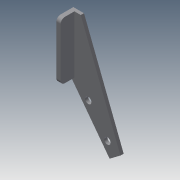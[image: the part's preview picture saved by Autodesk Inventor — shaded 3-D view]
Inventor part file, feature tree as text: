
AUTODESK INVENTOR PART (.ipt)
format: ipt  version: 2013 (Build 170138000, 138)  size: 157,184 bytes
history: native  units: mm
features: sketch x13, extrude x8, fillet x2
ambient origin geometry x8: Origin, YZ Plane, XZ Plane, XY Plane, X Axis, Y Axis, Z Axis, Center Point
bodies: Solid1 (feature_tree)
feature tree (23):
  sketch  "Sketch1"  dims[d4=3.0mm d5=3.0mm d6=2.0mm d7=0.0mm]
  extrude  "Extrusion1"  Depth=2.0mm TaperAngle=0.0deg
  extrude  "Extrusion2"  Depth=2.0mm TaperAngle=0.0deg
  extrude  "Extrusion3"  Depth=2.0mm TaperAngle=0.0deg
  sketch  "Sketch5"  dims[d19=0.5mm d20=0.0mm d21=10.0mm]
  extrude  "Extrusion4"  Depth=6.0mm TaperAngle=0.0deg
  sketch  "Sketch7"  dims[d25=1.5mm d26=0.0mm d27=10.0mm d28=0.0mm]
  sketch  "Sketch8"  dims[d29=2.0mm d30=2.0mm]
  extrude  "Extrusion5"  Depth=10.0mm
  sketch  "Sketch10"
  extrude  "Extrusion6"  Depth=1.5mm TaperAngle=0.0deg
  extrude  "Extrusion7"  Depth=10.0mm TaperAngle=0.0deg
  extrude  "Extrusion8"  Depth=2.0mm
  fillet  "Fillet1"  [1 undecoded]
  fillet  "Fillet2"  [1 undecoded]
  sketch  "Sketch2"  dims[d8=10.0mm d11=2.0mm d12=0.0mm]
  sketch  "Sketch3"  dims[d13=5.0mm d14=2.0mm d15=0.0mm]
  sketch  "Sketch4"  dims[d16=2.0mm d17=6.0mm d18=0.0mm]
  sketch  "Sketch6"  dims[d22=5.0mm d23=1.5mm d24=0.0mm]
  sketch  "Sketch9"
  sketch  "Sketch11"
  sketch  "Sketch12"
  sketch  "Sketch13"
note: 2 required parameter values undecoded (feature->parameter linkage not recoverable at this tier; creation-order binding heuristic only, values carry confidence <= 0.55)
